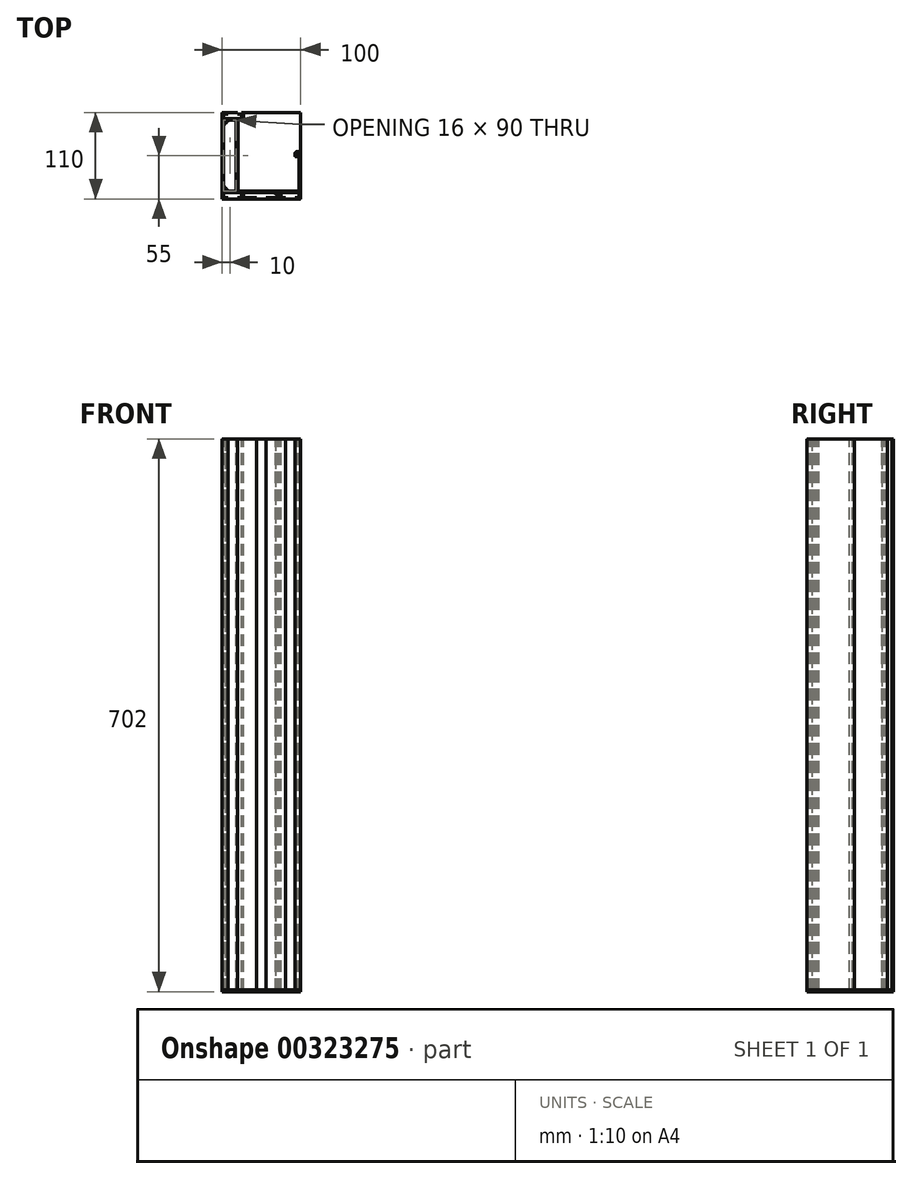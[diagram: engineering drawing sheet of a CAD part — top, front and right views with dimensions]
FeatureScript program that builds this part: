
annotation { "Feature Type Name" : "Feature", "Feature Type Description" : "" }
export const myFeature = defineFeature(function(context is Context, id is Id, definition is map)
    precondition{}
    {
        {
            var Q0;
            Q0=qCreatedBy(makeId("Top.planeOp"),FACE);
            var sketch = newSketch(context, id + "F0", { "sketchPlane" : qUnion([Q0])});
            skLineSegment(sketch, "E0", {"start": v(-2, 108) * mm, "end": v(-2, 2) * mm});
            skArc(sketch, "E1", {"start": v(0, 110) * mm, "mid": v(-1.41, 109.41) * mm, "end": v(-2, 108) * mm});
            skLineSegment(sketch, "E2", {"start": v(0, 108) * mm, "end": v(0, 102) * mm});
            skLineSegment(sketch, "E3", {"start": v(0, 94.94) * mm, "end": v(0, 15.06) * mm});
            skLineSegment(sketch, "E4", {"start": v(0, 8) * mm, "end": v(0, 2) * mm});
            skLineSegment(sketch, "E5", {"start": v(0, 0) * mm, "end": v(5.35, 0) * mm});
            skArc(sketch, "E6", {"start": v(-2, 2) * mm, "mid": v(-1.41, 0.59) * mm, "end": v(0, 0) * mm});
            skLineSegment(sketch, "E7", {"start": v(17.65, 0) * mm, "end": v(41.85, 0) * mm});
            skLineSegment(sketch, "E8", {"start": v(54.15, 0) * mm, "end": v(78.35, 0) * mm});
            skLineSegment(sketch, "E9", {"start": v(90.65, 0) * mm, "end": v(96, 0) * mm});
            skLineSegment(sketch, "E10", {"start": v(0, 2) * mm, "end": v(5.35, 2) * mm});
            skLineSegment(sketch, "E11", {"start": v(17.65, 2) * mm, "end": v(23, 2) * mm});
            skLineSegment(sketch, "E12", {"start": v(25, 2) * mm, "end": v(41.85, 2) * mm});
            skLineSegment(sketch, "E13", {"start": v(54.15, 2) * mm, "end": v(71, 2) * mm});
            skLineSegment(sketch, "E14", {"start": v(73, 2) * mm, "end": v(78.35, 2) * mm});
            skLineSegment(sketch, "E15", {"start": v(90.65, 2) * mm, "end": v(96, 2) * mm});
            skLineSegment(sketch, "E16", {"start": v(98, 2) * mm, "end": v(98, 58) * mm});
            skArc(sketch, "E17", {"start": v(98, 58) * mm, "mid": v(97.41, 59.41) * mm, "end": v(96, 60) * mm});
            skArc(sketch, "E18", {"start": v(96, 0) * mm, "mid": v(97.41, 0.59) * mm, "end": v(98, 2) * mm});
            skLineSegment(sketch, "E19", {"start": v(96, 2) * mm, "end": v(96, 8) * mm});
            skLineSegment(sketch, "E20", {"start": v(96, 12) * mm, "end": v(96, 53.87) * mm});
            skLineSegment(sketch, "E21", {"start": v(90.8, 54.28) * mm, "end": v(90.8, 58) * mm});
            skArc(sketch, "E22", {"start": v(90.8, 54.28) * mm, "mid": v(90.95, 53.92) * mm, "end": v(91.3, 53.78) * mm});
            skArc(sketch, "E23", {"start": v(94, 10) * mm, "mid": v(95.41, 10.59) * mm, "end": v(96, 12) * mm});
            skLineSegment(sketch, "E24", {"start": v(0, 110) * mm, "end": v(5.35, 110) * mm});
            skLineSegment(sketch, "E25", {"start": v(17.65, 110) * mm, "end": v(23, 110) * mm});
            skLineSegment(sketch, "E26", {"start": v(0, 108) * mm, "end": v(5.35, 108) * mm});
            skLineSegment(sketch, "E27", {"start": v(17.65, 108) * mm, "end": v(23, 108) * mm});
            skLineSegment(sketch, "E28", {"start": v(25, 108) * mm, "end": v(25, 102) * mm});
            skArc(sketch, "E29", {"start": v(25, 108) * mm, "mid": v(24.41, 109.41) * mm, "end": v(23, 110) * mm});
            skLineSegment(sketch, "E30", {"start": v(23, 108) * mm, "end": v(23, 102) * mm});
            skLineSegment(sketch, "E31", {"start": v(23, 100) * mm, "end": v(18, 100) * mm});
            skArc(sketch, "E32", {"start": v(23, 100) * mm, "mid": v(24.41, 100.59) * mm, "end": v(25, 102) * mm});
            skLineSegment(sketch, "E33", {"start": v(16, 100) * mm, "end": v(5.06, 100) * mm});
            skLineSegment(sketch, "E34", {"start": v(23, 102) * mm, "end": v(0, 102) * mm});
            skLineSegment(sketch, "E35", {"start": v(94, 10) * mm, "end": v(20, 10) * mm});
            skArc(sketch, "E36", {"start": v(18, 12) * mm, "mid": v(18.59, 10.59) * mm, "end": v(20, 10) * mm});
            skLineSegment(sketch, "E37", {"start": v(16, 10) * mm, "end": v(5.06, 10) * mm});
            skLineSegment(sketch, "E38", {"start": v(96, 8) * mm, "end": v(73, 8) * mm});
            skLineSegment(sketch, "E39", {"start": v(65.94, 8) * mm, "end": v(25, 8) * mm});
            skLineSegment(sketch, "E40", {"start": v(23, 8) * mm, "end": v(0, 8) * mm});
            skLineSegment(sketch, "E41", {"start": v(18, 12) * mm, "end": v(18, 100) * mm});
            skLineSegment(sketch, "E42", {"start": v(16, 10) * mm, "end": v(16, 100) * mm});
            skLineSegment(sketch, "E43", {"start": v(25, 8) * mm, "end": v(25, 2) * mm});
            skLineSegment(sketch, "E44", {"start": v(23, 8) * mm, "end": v(23, 2) * mm});
            skLineSegment(sketch, "E45", {"start": v(71, 2.94) * mm, "end": v(71, 2) * mm});
            skLineSegment(sketch, "E46", {"start": v(73, 8) * mm, "end": v(73, 2) * mm});
            skLineSegment(sketch, "E47", {"start": v(17.65, 110) * mm, "end": v(17.65, 108) * mm});
            skLineSegment(sketch, "E48", {"start": v(5.35, 110) * mm, "end": v(5.35, 108) * mm});
            skLineSegment(sketch, "E49", {"start": v(17.65, 2) * mm, "end": v(17.65, 0) * mm});
            skLineSegment(sketch, "E50", {"start": v(5.35, 2) * mm, "end": v(5.35, 0) * mm});
            skLineSegment(sketch, "E51", {"start": v(90.65, 2) * mm, "end": v(90.65, 0) * mm});
            skLineSegment(sketch, "E52", {"start": v(78.35, 2) * mm, "end": v(78.35, 0) * mm});
            skLineSegment(sketch, "E53", {"start": v(96, 60) * mm, "end": v(92.8, 60) * mm});
            skArc(sketch, "E54", {"start": v(92.8, 60) * mm, "mid": v(91.39, 59.41) * mm, "end": v(90.8, 58) * mm});
            skArc(sketch, "E55", {"start": v(3.2, 98.57) * mm, "mid": v(0.47, 99.53) * mm, "end": v(1.43, 96.8) * mm});
            skLineSegment(sketch, "E56", {"start": v(4.6, 99.3) * mm, "end": v(4.96, 98.51) * mm});
            skArc(sketch, "E57", {"start": v(5.06, 100) * mm, "mid": v(4.64, 99.77) * mm, "end": v(4.6, 99.3) * mm});
            skArc(sketch, "E58", {"start": v(4.82, 97.92) * mm, "mid": v(5, 98.2) * mm, "end": v(4.96, 98.51) * mm});
            skArc(sketch, "E59", {"start": v(3.2, 98.58) * mm, "mid": v(3.81, 97.76) * mm, "end": v(4.82, 97.92) * mm});
            skArc(sketch, "E60", {"start": v(2.08, 95.18) * mm, "mid": v(2.24, 96.19) * mm, "end": v(1.42, 96.8) * mm});
            skArc(sketch, "E61", {"start": v(1.5, 95.04) * mm, "mid": v(1.81, 95.01) * mm, "end": v(2.08, 95.18) * mm});
            skLineSegment(sketch, "E62", {"start": v(1.5, 95.04) * mm, "end": v(0.7, 95.4) * mm});
            skLineSegment(sketch, "E63", {"start": v(5.06, 100) * mm, "end": v(6.06, 100) * mm});
            skLineSegment(sketch, "E64", {"start": v(0, 86.97) * mm, "end": v(0, 85.72) * mm});
            skArc(sketch, "E65", {"start": v(0.7, 95.4) * mm, "mid": v(0.23, 95.36) * mm, "end": v(0, 94.94) * mm});
            skArc(sketch, "E66", {"start": v(1.43, 13.2) * mm, "mid": v(0.47, 10.47) * mm, "end": v(3.2, 11.43) * mm});
            skLineSegment(sketch, "E67", {"start": v(4.6, 10.7) * mm, "end": v(4.96, 11.49) * mm});
            skArc(sketch, "E68", {"start": v(4.6, 10.7) * mm, "mid": v(4.64, 10.23) * mm, "end": v(5.06, 10) * mm});
            skArc(sketch, "E69", {"start": v(4.96, 11.49) * mm, "mid": v(5, 11.8) * mm, "end": v(4.82, 12.08) * mm});
            skArc(sketch, "E70", {"start": v(4.82, 12.08) * mm, "mid": v(3.81, 12.24) * mm, "end": v(3.2, 11.42) * mm});
            skArc(sketch, "E71", {"start": v(1.42, 13.2) * mm, "mid": v(2.24, 13.81) * mm, "end": v(2.08, 14.82) * mm});
            skArc(sketch, "E72", {"start": v(2.08, 14.82) * mm, "mid": v(1.81, 14.99) * mm, "end": v(1.5, 14.96) * mm});
            skLineSegment(sketch, "E73", {"start": v(1.5, 14.96) * mm, "end": v(0.7, 14.6) * mm});
            skArc(sketch, "E74", {"start": v(0, 15.06) * mm, "mid": v(0.23, 14.64) * mm, "end": v(0.7, 14.6) * mm});
            skArc(sketch, "E75", {"start": v(69.57, 4.8) * mm, "mid": v(70.53, 7.53) * mm, "end": v(67.8, 6.57) * mm});
            skLineSegment(sketch, "E76", {"start": v(70.3, 3.4) * mm, "end": v(69.51, 3.04) * mm});
            skArc(sketch, "E77", {"start": v(71, 2.94) * mm, "mid": v(70.77, 3.36) * mm, "end": v(70.3, 3.4) * mm});
            skArc(sketch, "E78", {"start": v(68.92, 3.18) * mm, "mid": v(69.2, 3) * mm, "end": v(69.51, 3.04) * mm});
            skArc(sketch, "E79", {"start": v(69.58, 4.8) * mm, "mid": v(68.76, 4.19) * mm, "end": v(68.92, 3.18) * mm});
            skArc(sketch, "E80", {"start": v(66.18, 5.92) * mm, "mid": v(67.19, 5.76) * mm, "end": v(67.8, 6.58) * mm});
            skArc(sketch, "E81", {"start": v(66.04, 6.5) * mm, "mid": v(66.01, 6.19) * mm, "end": v(66.18, 5.92) * mm});
            skLineSegment(sketch, "E82", {"start": v(66.04, 6.5) * mm, "end": v(66.4, 7.3) * mm});
            skArc(sketch, "E83", {"start": v(66.4, 7.3) * mm, "mid": v(66.36, 7.77) * mm, "end": v(65.94, 8) * mm});
            skArc(sketch, "E84", {"start": v(95.65, 55.4) * mm, "mid": v(94.4, 58) * mm, "end": v(93.15, 55.4) * mm});
            skArc(sketch, "E85", {"start": v(95.65, 55.4) * mm, "mid": v(95.46, 54.55) * mm, "end": v(96, 53.87) * mm});
            skArc(sketch, "E86", {"start": v(92.37, 53.78) * mm, "mid": v(93.27, 54.34) * mm, "end": v(93.15, 55.4) * mm});
            skLineSegment(sketch, "E87", {"start": v(92.37, 53.78) * mm, "end": v(91.3, 53.78) * mm});
            skLineSegment(sketch, "E88", {"start": v(41.85, 2) * mm, "end": v(41.85, 0) * mm});
            skLineSegment(sketch, "E89", {"start": v(54.15, 2) * mm, "end": v(54.15, 0) * mm});
            skSolve(sketch);
        }
        {
            var Q0;
            Q0=makeQuery(id+"F0.imprint","IMPRINT",FACE,{"disambiguationData":[TD([[makeQuery(id+"F0.imprint","IMPRINT",EDGE,{"derivedFrom":sQuery(id+"F0.wireOp",EDGE,"E0")}),1.0]])]});
            extrude(context, id + "F1", {"entities" : qUnion([Q0]), "oppositeDirection" : true, "depth" : 700 * mm});
        }
        {
            var Q0;
            Q0=makeQuery(id+"F1.opExtrude","CAP_FACE",FACE,{"disambiguationData":[OSD([sQuery(id+"F0.wireOp",EDGE,"E0"),sQuery(id+"F0.wireOp",EDGE,"E1"),sQuery(id+"F0.wireOp",EDGE,"E2"),sQuery(id+"F0.wireOp",EDGE,"E3"),sQuery(id+"F0.wireOp",EDGE,"E4"),sQuery(id+"F0.wireOp",EDGE,"E5"),sQuery(id+"F0.wireOp",EDGE,"E6"),sQuery(id+"F0.wireOp",EDGE,"E7"),sQuery(id+"F0.wireOp",EDGE,"E8"),sQuery(id+"F0.wireOp",EDGE,"E9"),sQuery(id+"F0.wireOp",EDGE,"E10"),sQuery(id+"F0.wireOp",EDGE,"E11"),sQuery(id+"F0.wireOp",EDGE,"E12"),sQuery(id+"F0.wireOp",EDGE,"E13"),sQuery(id+"F0.wireOp",EDGE,"E14"),sQuery(id+"F0.wireOp",EDGE,"E15"),sQuery(id+"F0.wireOp",EDGE,"E16"),sQuery(id+"F0.wireOp",EDGE,"E17"),sQuery(id+"F0.wireOp",EDGE,"E18"),sQuery(id+"F0.wireOp",EDGE,"E19"),sQuery(id+"F0.wireOp",EDGE,"E20"),sQuery(id+"F0.wireOp",EDGE,"E21"),sQuery(id+"F0.wireOp",EDGE,"E22"),sQuery(id+"F0.wireOp",EDGE,"E23"),sQuery(id+"F0.wireOp",EDGE,"E24"),sQuery(id+"F0.wireOp",EDGE,"E25"),sQuery(id+"F0.wireOp",EDGE,"E26"),sQuery(id+"F0.wireOp",EDGE,"E27"),sQuery(id+"F0.wireOp",EDGE,"E28"),sQuery(id+"F0.wireOp",EDGE,"E29"),sQuery(id+"F0.wireOp",EDGE,"E30"),sQuery(id+"F0.wireOp",EDGE,"E31"),sQuery(id+"F0.wireOp",EDGE,"E32"),sQuery(id+"F0.wireOp",EDGE,"E33"),sQuery(id+"F0.wireOp",EDGE,"E34"),sQuery(id+"F0.wireOp",EDGE,"E35"),sQuery(id+"F0.wireOp",EDGE,"E36"),sQuery(id+"F0.wireOp",EDGE,"E37"),sQuery(id+"F0.wireOp",EDGE,"E38"),sQuery(id+"F0.wireOp",EDGE,"E39"),sQuery(id+"F0.wireOp",EDGE,"E40"),sQuery(id+"F0.wireOp",EDGE,"E41"),sQuery(id+"F0.wireOp",EDGE,"E42"),sQuery(id+"F0.wireOp",EDGE,"E43"),sQuery(id+"F0.wireOp",EDGE,"E44"),sQuery(id+"F0.wireOp",EDGE,"E45"),sQuery(id+"F0.wireOp",EDGE,"E46"),sQuery(id+"F0.wireOp",EDGE,"E47"),sQuery(id+"F0.wireOp",EDGE,"E48"),sQuery(id+"F0.wireOp",EDGE,"E49"),sQuery(id+"F0.wireOp",EDGE,"E50"),sQuery(id+"F0.wireOp",EDGE,"E51"),sQuery(id+"F0.wireOp",EDGE,"E52"),sQuery(id+"F0.wireOp",EDGE,"E53"),sQuery(id+"F0.wireOp",EDGE,"E54"),sQuery(id+"F0.wireOp",EDGE,"E55"),sQuery(id+"F0.wireOp",EDGE,"E56"),sQuery(id+"F0.wireOp",EDGE,"E57"),sQuery(id+"F0.wireOp",EDGE,"E58"),sQuery(id+"F0.wireOp",EDGE,"E59"),sQuery(id+"F0.wireOp",EDGE,"E60"),sQuery(id+"F0.wireOp",EDGE,"E61"),sQuery(id+"F0.wireOp",EDGE,"E62"),sQuery(id+"F0.wireOp",EDGE,"E63"),sQuery(id+"F0.wireOp",EDGE,"E64"),sQuery(id+"F0.wireOp",EDGE,"E65"),sQuery(id+"F0.wireOp",EDGE,"E66"),sQuery(id+"F0.wireOp",EDGE,"E67"),sQuery(id+"F0.wireOp",EDGE,"E68"),sQuery(id+"F0.wireOp",EDGE,"E69"),sQuery(id+"F0.wireOp",EDGE,"E70"),sQuery(id+"F0.wireOp",EDGE,"E71"),sQuery(id+"F0.wireOp",EDGE,"E72"),sQuery(id+"F0.wireOp",EDGE,"E73"),sQuery(id+"F0.wireOp",EDGE,"E74"),sQuery(id+"F0.wireOp",EDGE,"E75"),sQuery(id+"F0.wireOp",EDGE,"E76"),sQuery(id+"F0.wireOp",EDGE,"E77"),sQuery(id+"F0.wireOp",EDGE,"E78"),sQuery(id+"F0.wireOp",EDGE,"E79"),sQuery(id+"F0.wireOp",EDGE,"E80"),sQuery(id+"F0.wireOp",EDGE,"E81"),sQuery(id+"F0.wireOp",EDGE,"E82"),sQuery(id+"F0.wireOp",EDGE,"E83"),sQuery(id+"F0.wireOp",EDGE,"E84"),sQuery(id+"F0.wireOp",EDGE,"E85"),sQuery(id+"F0.wireOp",EDGE,"E86"),sQuery(id+"F0.wireOp",EDGE,"E87"),sQuery(id+"F0.wireOp",EDGE,"E88"),sQuery(id+"F0.wireOp",EDGE,"E89")])],"isStart":false});
            var sketch = newSketch(context, id + "F2", { "sketchPlane" : qUnion([Q0])});
            skLineSegment(sketch, "E90.bottom", {"start": v(98, -110) * mm, "end": v(-2, -110) * mm});
            skLineSegment(sketch, "E90.top", {"start": v(98, 0) * mm, "end": v(-2, 0) * mm});
            skLineSegment(sketch, "E90.left", {"start": v(98, -110) * mm, "end": v(98, 0) * mm});
            skLineSegment(sketch, "E90.right", {"start": v(-2, -110) * mm, "end": v(-2, 0) * mm});
            skSolve(sketch);
        }
        {
            var Q0;
            Q0 = qSketchRegion(id + "F2", true);
            extrude(context, id + "F3", {"entities" : qUnion([Q0]), "depth" : 2 * mm});
        }
        {
            var Q0;
            Q0=makeQuery(id+"F3.opExtrude","CAP_FACE",FACE,{"disambiguationData":[OSD([sQuery(id+"F2.wireOp",EDGE,"E90.bottom"),sQuery(id+"F2.wireOp",EDGE,"E90.top"),sQuery(id+"F2.wireOp",EDGE,"E90.left"),sQuery(id+"F2.wireOp",EDGE,"E90.right")])],"isStart":false});
            var sketch = newSketch(context, id + "F4", { "sketchPlane" : qUnion([Q0])});
            skLineSegment(sketch, "E91", {"start": v(98, -95.2) * mm, "end": v(82.77, -110) * mm});
            skSolve(sketch);
        }
        {
            var Q0;
            Q0=makeQuery(id+"F1.opExtrude","CAP_FACE",FACE,{"disambiguationData":[OSD([sQuery(id+"F0.wireOp",EDGE,"E0"),sQuery(id+"F0.wireOp",EDGE,"E1"),sQuery(id+"F0.wireOp",EDGE,"E2"),sQuery(id+"F0.wireOp",EDGE,"E3"),sQuery(id+"F0.wireOp",EDGE,"E4"),sQuery(id+"F0.wireOp",EDGE,"E5"),sQuery(id+"F0.wireOp",EDGE,"E6"),sQuery(id+"F0.wireOp",EDGE,"E7"),sQuery(id+"F0.wireOp",EDGE,"E8"),sQuery(id+"F0.wireOp",EDGE,"E9"),sQuery(id+"F0.wireOp",EDGE,"E10"),sQuery(id+"F0.wireOp",EDGE,"E11"),sQuery(id+"F0.wireOp",EDGE,"E12"),sQuery(id+"F0.wireOp",EDGE,"E13"),sQuery(id+"F0.wireOp",EDGE,"E14"),sQuery(id+"F0.wireOp",EDGE,"E15"),sQuery(id+"F0.wireOp",EDGE,"E16"),sQuery(id+"F0.wireOp",EDGE,"E17"),sQuery(id+"F0.wireOp",EDGE,"E18"),sQuery(id+"F0.wireOp",EDGE,"E19"),sQuery(id+"F0.wireOp",EDGE,"E20"),sQuery(id+"F0.wireOp",EDGE,"E21"),sQuery(id+"F0.wireOp",EDGE,"E22"),sQuery(id+"F0.wireOp",EDGE,"E23"),sQuery(id+"F0.wireOp",EDGE,"E24"),sQuery(id+"F0.wireOp",EDGE,"E25"),sQuery(id+"F0.wireOp",EDGE,"E26"),sQuery(id+"F0.wireOp",EDGE,"E27"),sQuery(id+"F0.wireOp",EDGE,"E28"),sQuery(id+"F0.wireOp",EDGE,"E29"),sQuery(id+"F0.wireOp",EDGE,"E30"),sQuery(id+"F0.wireOp",EDGE,"E31"),sQuery(id+"F0.wireOp",EDGE,"E32"),sQuery(id+"F0.wireOp",EDGE,"E33"),sQuery(id+"F0.wireOp",EDGE,"E34"),sQuery(id+"F0.wireOp",EDGE,"E35"),sQuery(id+"F0.wireOp",EDGE,"E36"),sQuery(id+"F0.wireOp",EDGE,"E37"),sQuery(id+"F0.wireOp",EDGE,"E38"),sQuery(id+"F0.wireOp",EDGE,"E39"),sQuery(id+"F0.wireOp",EDGE,"E40"),sQuery(id+"F0.wireOp",EDGE,"E41"),sQuery(id+"F0.wireOp",EDGE,"E42"),sQuery(id+"F0.wireOp",EDGE,"E43"),sQuery(id+"F0.wireOp",EDGE,"E44"),sQuery(id+"F0.wireOp",EDGE,"E45"),sQuery(id+"F0.wireOp",EDGE,"E46"),sQuery(id+"F0.wireOp",EDGE,"E47"),sQuery(id+"F0.wireOp",EDGE,"E48"),sQuery(id+"F0.wireOp",EDGE,"E49"),sQuery(id+"F0.wireOp",EDGE,"E50"),sQuery(id+"F0.wireOp",EDGE,"E51"),sQuery(id+"F0.wireOp",EDGE,"E52"),sQuery(id+"F0.wireOp",EDGE,"E53"),sQuery(id+"F0.wireOp",EDGE,"E54"),sQuery(id+"F0.wireOp",EDGE,"E55"),sQuery(id+"F0.wireOp",EDGE,"E56"),sQuery(id+"F0.wireOp",EDGE,"E57"),sQuery(id+"F0.wireOp",EDGE,"E58"),sQuery(id+"F0.wireOp",EDGE,"E59"),sQuery(id+"F0.wireOp",EDGE,"E60"),sQuery(id+"F0.wireOp",EDGE,"E61"),sQuery(id+"F0.wireOp",EDGE,"E62"),sQuery(id+"F0.wireOp",EDGE,"E63"),sQuery(id+"F0.wireOp",EDGE,"E64"),sQuery(id+"F0.wireOp",EDGE,"E65"),sQuery(id+"F0.wireOp",EDGE,"E66"),sQuery(id+"F0.wireOp",EDGE,"E67"),sQuery(id+"F0.wireOp",EDGE,"E68"),sQuery(id+"F0.wireOp",EDGE,"E69"),sQuery(id+"F0.wireOp",EDGE,"E70"),sQuery(id+"F0.wireOp",EDGE,"E71"),sQuery(id+"F0.wireOp",EDGE,"E72"),sQuery(id+"F0.wireOp",EDGE,"E73"),sQuery(id+"F0.wireOp",EDGE,"E74"),sQuery(id+"F0.wireOp",EDGE,"E75"),sQuery(id+"F0.wireOp",EDGE,"E76"),sQuery(id+"F0.wireOp",EDGE,"E77"),sQuery(id+"F0.wireOp",EDGE,"E78"),sQuery(id+"F0.wireOp",EDGE,"E79"),sQuery(id+"F0.wireOp",EDGE,"E80"),sQuery(id+"F0.wireOp",EDGE,"E81"),sQuery(id+"F0.wireOp",EDGE,"E82"),sQuery(id+"F0.wireOp",EDGE,"E83"),sQuery(id+"F0.wireOp",EDGE,"E84"),sQuery(id+"F0.wireOp",EDGE,"E85"),sQuery(id+"F0.wireOp",EDGE,"E86"),sQuery(id+"F0.wireOp",EDGE,"E87"),sQuery(id+"F0.wireOp",EDGE,"E88"),sQuery(id+"F0.wireOp",EDGE,"E89")])],"isStart":true});
            var sketch = newSketch(context, id + "F5", { "sketchPlane" : qUnion([Q0])});
            skLineSegment(sketch, "E92.0", {"start": v(23, 100) * mm, "end": v(18, 100) * mm});
            skArc(sketch, "E93.0", {"start": v(23, 100) * mm, "mid": v(24.41, 100.59) * mm, "end": v(25, 102) * mm});
            skLineSegment(sketch, "E94.0", {"start": v(25, 108) * mm, "end": v(25, 102) * mm});
            skArc(sketch, "E95.0", {"start": v(25, 108) * mm, "mid": v(24.41, 109.41) * mm, "end": v(23, 110) * mm});
            skLineSegment(sketch, "E96.0", {"start": v(17.65, 110) * mm, "end": v(23, 110) * mm});
            skLineSegment(sketch, "E97.0", {"start": v(17.65, 110) * mm, "end": v(17.65, 108) * mm});
            skLineSegment(sketch, "E98.0", {"start": v(17.65, 108) * mm, "end": v(23, 108) * mm});
            skLineSegment(sketch, "E99.0", {"start": v(23, 108) * mm, "end": v(23, 102) * mm});
            skLineSegment(sketch, "E100.0", {"start": v(23, 102) * mm, "end": v(18, 102) * mm});
            skLineSegment(sketch, "E101", {"start": v(18, 100) * mm, "end": v(18, 102) * mm});
            skPoint(sketch, "E102.orphan", {"position": v(0, 102) * mm});
            skSolve(sketch);
        }
        {
            var Q0;
            Q0 = qSketchRegion(id + "F5", true);
            extrude(context, id + "F6", {"entities" : qUnion([Q0]), "operationType" : NewBodyOperationType.REMOVE, "endBound" : BoundingType.THROUGH_ALL, "oppositeDirection" : true, "depth" : 25 * mm});
        }
    });
